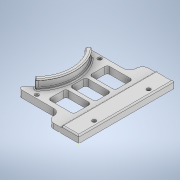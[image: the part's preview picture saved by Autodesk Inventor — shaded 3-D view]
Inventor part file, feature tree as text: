
AUTODESK INVENTOR PART (.ipt)
format: ipt  version: 2022 (Build 260153000, 153)  size: 4,515,840 bytes
history: native  units: in
note: dims shown in document units (in); Inventor stores cm internally (conversion verified against a paired STEP export)
features: sketch x19, extrude x13, fillet x9, hole x2, sweep x2, plane x1, mirror x1, chamfer x1
ambient origin geometry x8: Origin, YZ Plane, XZ Plane, XY Plane, X Axis, Y Axis, Z Axis, Center Point
bodies: Solid1 (feature_tree)
feature tree (48):
  extrude  "Extrusion1"  Depth=2.9685in
  sketch  "Sketch3"  dims[d2=0.1575in d3=0.0in d5=1.7008in d15=0.1181in]
  extrude  "Extrusion2"  Depth=0.1181in
  plane  "Work Plane1"
  fillet  "Fillet1"  Radius=0.1181in
  mirror  "Mirror1"
  extrude  "Extrusion4"  Depth=0.1181in
  extrude  "Extrusion5"  Depth=0.1575in
  hole  "Hole2"  [1 undecoded]
  fillet  "Fillet2"  Radius=0.1181in
  extrude  "Extrusion8"  Depth=0.0394in
  fillet  "Fillet7"  Radius=0.2992in
  extrude  "Extrusion9"  Depth=0.5512in
  extrude  "Extrusion10"  Depth=0.0394in
  extrude  "Extrusion15"  Depth=0.3937in
  sketch  "Sketch24"  dims[d44=0.1181in d45=0.2362in d46=0.1575in d47=0.0787in d48=90.0deg d49=0.315in d50=0.8108in d51=0.0394in]
  fillet  "Fillet17"  Radius=0.3937in
  sketch  "Sketch27"  dims[d85=1.2598in d86=1.4843in d89=0.3937in d90=0.0in]
  sweep  "Sweep7"
  sweep  "Sweep9"
  hole  "Hole4"  [1 undecoded]
  chamfer  "Chamfer2"  Distance=0.2953in
  extrude  "Extrusion18"  Depth=0.0394in
  fillet  "Fillet25"  Radius=0.2008in
  extrude  "Extrusion19"  Depth=0.0787in
  fillet  "Fillet26"  Radius=0.0315in
  sketch  "Sketch34"  dims[d188=2.5433in]
  extrude  "Extrusion20"  TaperAngle=0.0deg  [1 undecoded]
  fillet  "Fillet27"  Radius=0.6339in
  extrude  "Extrusion21"  Depth=0.0787in
  fillet  "Fillet29"  Radius=0.1575in
  extrude  "Extrusion22"  Depth=0.0787in
  fillet  "Fillet30"  Radius=0.2008in
  sketch  "Sketch2"  dims[d0=1.6142in d1=2.9685in]
  sketch  "Sketch4"  dims[d16=0.1181in d18=0.1457in]
  sketch  "Sketch7"  dims[d19=0.1575in d20=0.1575in]
  sketch  "Sketch10"  dims[d21=0.0984in d22=0.7874in d24=2.5669in d25=0.3937in d27=0.3937in d29=0.1181in d30=0.0in]
  sketch  "Sketch11"  dims[d36=0.0394in d37=0.1102in d38=0.2992in]
  sketch  "Sketch12"  dims[d39=0.0591in d40=0.0in d41=0.5512in]
  sketch  "Sketch23"  dims[d42=0.0591in d43=0.0in]
  sketch  "3D Sketch7"
  sketch  "Sketch29"  dims[d91=0.0787in d93=1.0236in]
  sketch  "3D Sketch9"
  sketch  "Sketch31"  dims[d95=0.4016in d96=0.0in d97=1.0236in]
  sketch  "Sketch32"  dims[d99=0.4016in d100=0.0in d167=2.2677in]
  sketch  "Sketch33"  dims[d168=2.1654in]
  sketch  "Sketch35"  dims[d189=1.5748in]
  sketch  "Sketch37"  dims[d190=0.3022in d191=0.2953in d192=0.0in d193=0.0394in d194=0.2008in d195=0.0374in d200=0.0315in d218=0.0in d219=0.0in d222=0.6339in d223=0.6339in d224=0.1575in d229=0.0433in d230=0.2008in d231=0.0374in d232=0.0in d233=0.0in d234=0.098in d245=0.379in d248=0.379in d249=0.1018in d250=0.0866in d251=0.2362in d252=0.1575in d253=0.0787in d254=90.0deg d255=0.315in d256=0.8108in d257=0.0197in d258=0.0787in d259=45.0deg d260=0.1018in d269=0.1181in d270=0.0in d273=2.4252in d274=0.0394in d278=0.3937in d279=0.0in d280=0.1181in d283=0.9409in d285=0.1811in d286=0.9409in d288=0.4016in d289=0.4016in d290=0.1575in d291=0.3937in d292=0.0in d293=0.1969in d296=0.2559in d297=0.9409in d298=0.9409in d299=0.1575in d300=0.0in d301=0.0787in d302=1.8504in d303=0.7244in d304=0.5591in d305=0.7976in d306=0.1181in d307=0.1181in d308=0.5577in d309=0.4987in d310=0.3937in d311=0.0in d312=0.0787in d52=0.8108in d53=0.0025in d54=0.0295in d55=0.0148in d140=0.0in d141=0.0in d142=0.0in d143=0.0in d144=0.0344in d237=0.0in d238=0.0in d239=0.0in d240=0.0in]
note: 3 required parameter values undecoded (feature->parameter linkage not recoverable at this tier; creation-order binding heuristic only, values carry confidence <= 0.55)
